# Revit family: PD4-GH-AP types Avec hôte
name_source: partatom
category: Dispositifs d'éclairage
units: mm (PartAtom-declared; Revit-internal decimal feet)

## family parameters
Conserver l'orientation des annotations = Oui
Cote de connecteur circulaire = Utiliser le diamètre
Couper avec des vides une fois chargée = Non
Hôte = Face
Partagée = Non
Point de calcul de pièce = Non
Type d'élément = Normal

## types (9) — shared parameters
Classe = II
Code d'assemblage = D5010200
Fabricant = B.E.G.
Hauteur de montage max = 1400 cm
Image du type = 360°.jpg
Marque = LUXOMAT
Mode de pose = Saillie
URL = http://www.luxomat.com
zero-valued in all types: Elévation par défaut

## per-type parameters (varying)
| type | Alimentation | Charge Cos ɸ =0.5 | Charge Cos ɸ =1 | Charge LED | Commentaires du type | Consommation | IP | Modèle | Relais | Référence | Température ambiante | Type de Sortie |
| 01- PD4-GH-AP Générique | 110-240 V AC |  |  |  | DET.PRES.GRANDE HAUTEUR.360°/Ø30M APPARENT |  | 20 ou 54 avec Socle IP54 | PD4-GH-AP |  |  | -25°C à +50°C |  |
| 02- PD4-M-1C-GH-AP réf 92245 | 110-240 V AC | 1150 VA | 2300 W | 300 W | DET.PRES.MAITRE.GRANDE HAUTEUR.1 CONTACT.360°/Ø30M APPARENT | 0,45 W | 20 ou 54 avec Socle IP54 | PD4-M-1C-GH-AP | 10 A | 92245 | -25°C à +50°C | TOR |
| 08- PD4-KNX-GH-DX-AP réf 93399 | 24 V DC par BUS KNX | 0 | 0 | 0 | DET.PRES.GRANDE HAUTEUR.KNX.VERSION DELUXE.360°/Ø30M APPARENT | 12 mA | 54 | PD4-KNX-GH-DX-AP | 0 | 93399 | -5°C à +45°C | KNX - 1 sortie Eclairage TOR ou GRADATION / 3 sorties Présence / Capteur de température |
| 04- PD4-S-GH-AP réf 92265 | 110-240 V AC | 0 | 0 | 0 | DET.PRES.ESCLAVE.GRANDE HAUTEUR.360°/Ø30M APPARENT | 0,25 W | 54 | PD4-S-GH-AP | 0 | 92265 | -25°C à +50°C | Esclave |
| 06- PD4-DALISYS-GH-AP réf 93345 | 10 à 22 V DC par BUS DALI | 0 | 0 | 0 | MULTI.CAPTEUR.PRES.GRANDE HAUTEUR.DALISYS.360°/Ø30M APPARENT | 7 mA | 54 | PD4-DALISYS-GH-AP | 0 | 93345 | -25°C à +50°C | DALI Adressable |
| 03- PD4-M-DACO-GH-AP réf 93469 | 110-240 V AC | 0 | 0 | 0 | DET.PRES.GRANDE HAUTEUR.DALI 2.360°/Ø30M APPARENT | 2 W | 54 | PD4-M-DACO-GH-AP | 0 | 93469 | -25°C à +50°C | DALI 2  (40 drivers maxi) |
| 05- PD4-DALILINK-GH-AP réf 93845 | 16V DC par bus DALI | 0 | 0 | 0 | MULTI.CAPTEUR.PRES.GRANDE HAUTEUR.DALILINK.360°/Ø30M APPARENT | 7 mA | 54 | PD4-DALILINK-GH-AP | 0 | 93845 | -25°C à +50°C | DALILINK |
| 07- PD4-BMS-DALI-2-GH-AP réf 93545 | 10 à 22 V DC par BUS DALI | 0 | 0 | 0 | MULTI.CAPTEUR.PRES.GRANDE HAUTEUR.BMS.DALI 2.360°/Ø30M APPARENT | 7 mA | 54 | PD4-BMS-DALI-2-GH-AP | 0 | 93545 | -25°C à +50°C | DALI 2 Adressable - BMS |
| 09- PD4-KNXs-GH-DX-AP réf 93518 | 24 V DC par BUS KNX | 0 | 0 | 0 | DET.PRES.GRANDE HAUTEUR.KNX Sécure.VERSION DELUXE.360°/Ø30M APPARENT | 12 mA | 54 | PD4-KNXs-GH-DX-AP | 0 | 93518 | -5°C à +45°C | KNX Sécure - 1 sortie Eclairage TOR ou GRADATION / 3 sorties Présence / Capteur de température / HCL |
